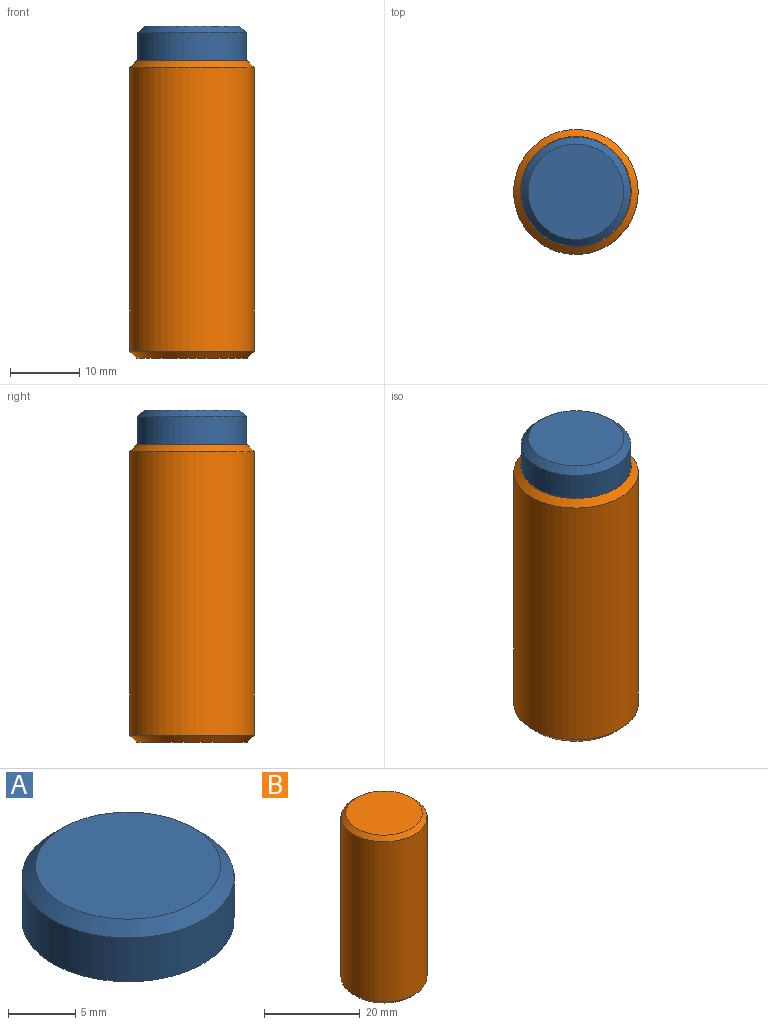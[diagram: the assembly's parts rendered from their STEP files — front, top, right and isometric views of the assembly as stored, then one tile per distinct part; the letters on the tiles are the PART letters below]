
ASSEMBLY  parts=2 mates=1
PART A: 4 faces, bbox 15.8x15.8x5 mm
  f0: cylinder r=7.9mm len=15.8mm, axis (0,0,-1), area 198.5mm2, adj f2,f3
  f1: plane 13.8x13.8mm, normal (0,0,1), area 149.6mm2, adj f3
  f2: plane 15.8x15.8mm, normal (0,0,-1), area 196.1mm2, adj f0
  f3: cone r=6.9mm half-angle=45deg, axis (0,0,-1), area 65.8mm2, adj f0,f1
PART B: 5 faces, bbox 18x18x43 mm
  f0: cylinder r=9mm len=41mm, axis (0,0,-1), area 2318.5mm2, adj f3,f4
  f1: plane 16x16mm, normal (0,0,1), area 201.1mm2, adj f4
  f2: plane 16x16mm, normal (0,0,-1), area 201.1mm2, adj f3
  f3: cone r=9mm half-angle=45deg, axis (0,0,1), area 75.5mm2, adj f0,f2
  f4: cone r=8mm half-angle=45deg, axis (0,0,-1), area 75.5mm2, adj f0,f1
PLACE A t=(-5.26,9.04,-5.88)mm
PLACE B t=(-5.26,9.04,-5.88)mm
MATE fastened B.f0 <-> A.f0  axis (0,0,1) through (-5.26,9.04,36.12)mm
